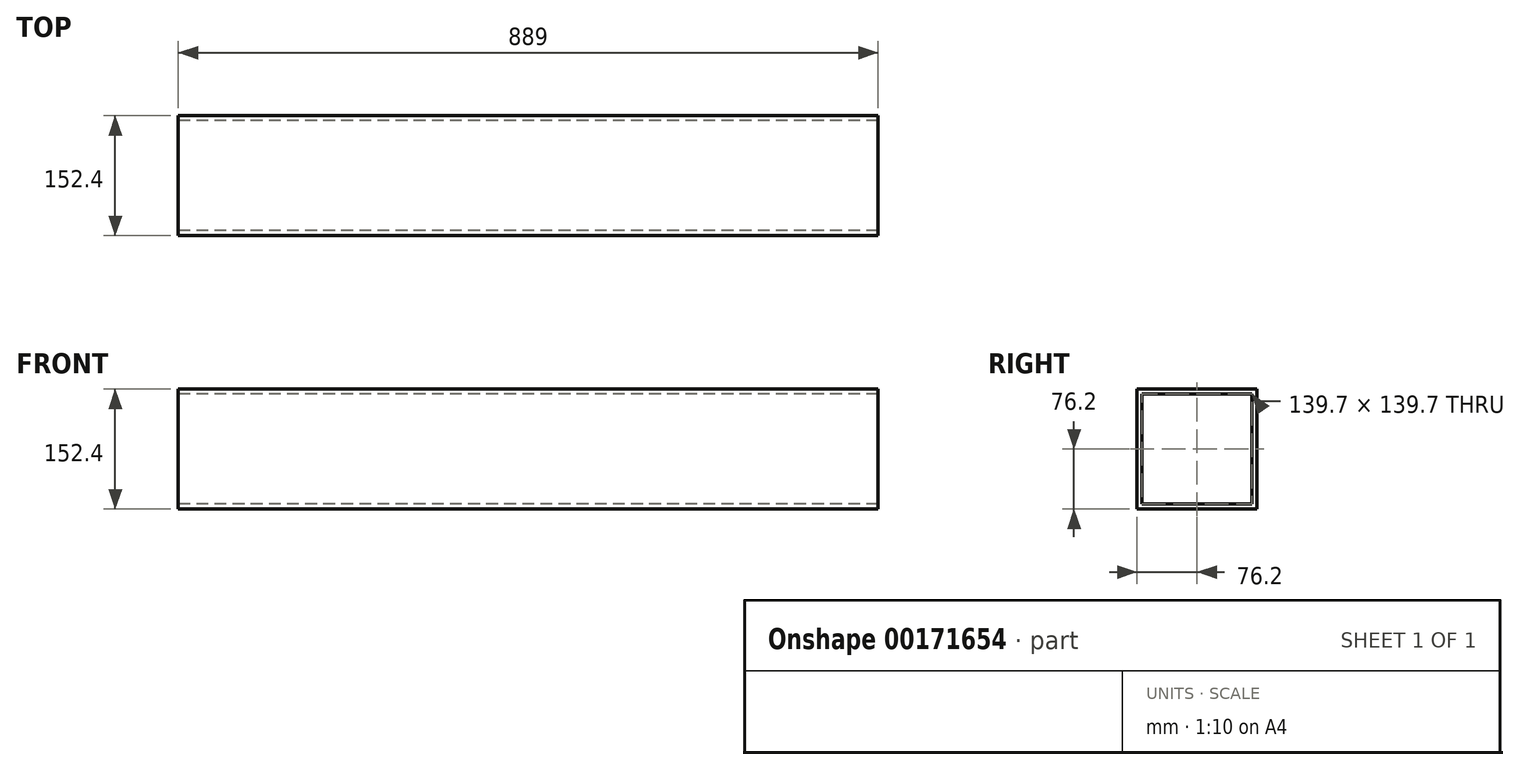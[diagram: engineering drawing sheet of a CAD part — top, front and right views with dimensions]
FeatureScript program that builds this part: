
annotation { "Feature Type Name" : "Feature", "Feature Type Description" : "" }
export const myFeature = defineFeature(function(context is Context, id is Id, definition is map)
    precondition{}
    {
        {
            var Q0;
            Q0=qCreatedBy(makeId("Right.planeOp"),FACE);
            var sketch = newSketch(context, id + "F0", { "sketchPlane" : qUnion([Q0])});
            skLineSegment(sketch, "E0.bottom", {"start": v(-76.2, 76.2) * mm, "end": v(76.2, 76.2) * mm});
            skLineSegment(sketch, "E0.top", {"start": v(-76.2, -76.2) * mm, "end": v(76.2, -76.2) * mm});
            skLineSegment(sketch, "E0.left", {"start": v(-76.2, 76.2) * mm, "end": v(-76.2, -76.2) * mm});
            skLineSegment(sketch, "E0.right", {"start": v(76.2, 76.2) * mm, "end": v(76.2, -76.2) * mm});
            skLineSegment(sketch, "E1.bottom", {"start": v(-69.85, 69.85) * mm, "end": v(69.85, 69.85) * mm});
            skLineSegment(sketch, "E1.top", {"start": v(-69.85, -69.85) * mm, "end": v(69.85, -69.85) * mm});
            skLineSegment(sketch, "E1.left", {"start": v(-69.85, 69.85) * mm, "end": v(-69.85, -69.85) * mm});
            skLineSegment(sketch, "E1.right", {"start": v(69.85, 69.85) * mm, "end": v(69.85, -69.85) * mm});
            skSolve(sketch);
        }
        {
            var Q0;
            Q0=makeQuery(id+"F0.imprint","IMPRINT",FACE,{"disambiguationData":[TD([[makeQuery(id+"F0.imprint","IMPRINT",EDGE,{"derivedFrom":sQuery(id+"F0.wireOp",EDGE,"E0.bottom")}),-1.0]])]});
            extrude(context, id + "F1", {"entities" : qUnion([Q0]), "depth" : 889 * mm});
        }
    });
